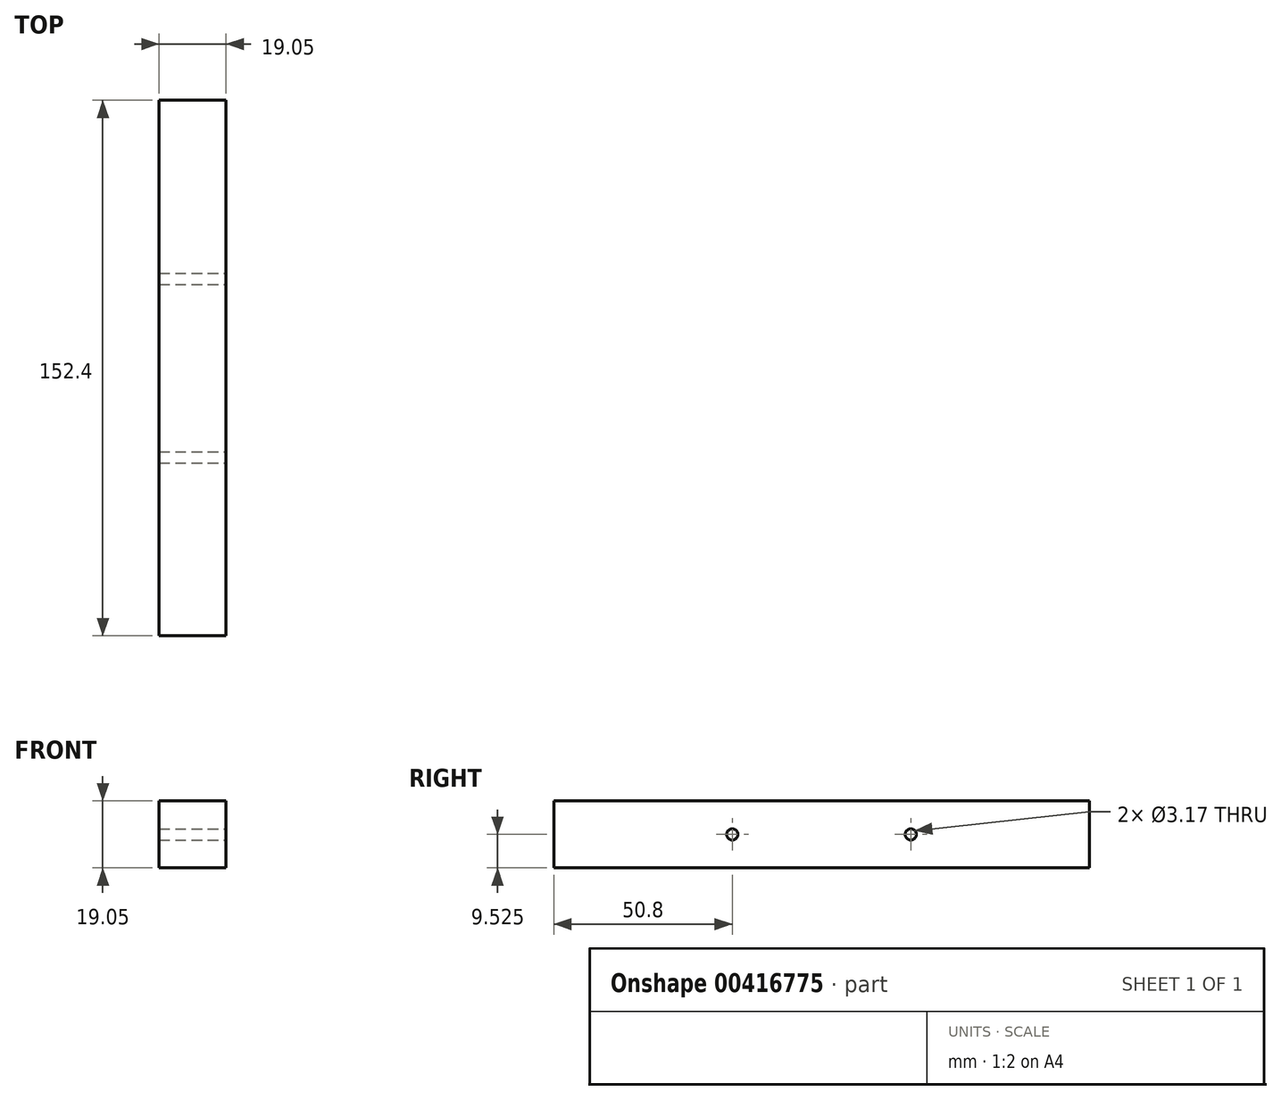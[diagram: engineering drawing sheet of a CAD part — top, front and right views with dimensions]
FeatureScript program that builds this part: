
annotation { "Feature Type Name" : "Feature", "Feature Type Description" : "" }
export const myFeature = defineFeature(function(context is Context, id is Id, definition is map)
    precondition{}
    {
        {
            var Q0;
            Q0=qCreatedBy(makeId("Front.planeOp"),FACE);
            var sketch = newSketch(context, id + "F0", { "sketchPlane" : qUnion([Q0])});
            skLineSegment(sketch, "E0.bottom", {"start": v(0, 0) * mm, "end": v(19.05, 0) * mm});
            skLineSegment(sketch, "E0.top", {"start": v(0, 19.05) * mm, "end": v(19.05, 19.05) * mm});
            skLineSegment(sketch, "E0.left", {"start": v(0, 0) * mm, "end": v(0, 19.05) * mm});
            skLineSegment(sketch, "E0.right", {"start": v(19.05, 0) * mm, "end": v(19.05, 19.05) * mm});
            skSolve(sketch);
        }
        {
            var Q0;
            Q0 = qSketchRegion(id + "F0", true);
            extrude(context, id + "F1", {"entities" : qUnion([Q0]), "depth" : 152.4 * mm});
        }
        {
            var Q0;
            Q0=makeQuery(id+"F1.opExtrude","SWEPT_FACE",FACE,{"disambiguationData":[OSD([sQuery(id+"F0.wireOp",EDGE,"E0.right")])]});
            var sketch = newSketch(context, id + "F2", { "sketchPlane" : qUnion([Q0])});
            skLineSegment(sketch, "E1", {"start": v(-152.4, 9.53) * mm, "end": v(0, 9.53) * mm, "construction": true});
            skCircle(sketch, "E2", {"center": v(-101.6, 9.53) * mm, "radius": 1.59 * mm});
            skCircle(sketch, "E3", {"center": v(-50.8, 9.52) * mm, "radius": 1.59 * mm});
            skSolve(sketch);
        }
        {
            var Q0;
            Q0 = qSketchRegion(id + "F2", true);
            extrude(context, id + "F3", {"entities" : qUnion([Q0]), "operationType" : NewBodyOperationType.REMOVE, "oppositeDirection" : true, "depth" : 25.4 * mm});
        }
    });
